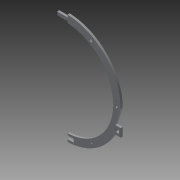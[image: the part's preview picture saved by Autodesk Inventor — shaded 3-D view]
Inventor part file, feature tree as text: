
AUTODESK INVENTOR PART (.ipt)
format: ipt  version: 2013 (Build 170138000, 138)  size: 147,968 bytes
history: native  units: in
note: dims shown in document units (in); Inventor stores cm internally (conversion verified against a paired STEP export)
features: extrude x1, sketch x1
ambient origin geometry x8: Origin, YZ Plane, XZ Plane, XY Plane, X Axis, Y Axis, Z Axis, Center Point
feature tree (2):
  extrude  "Extrusion21"  Depth=13.3in
  sketch  "Sketch1"  dims[d51=11.5in d52=13.3in d72=0.25in d73=0.2in d75=1.25in d76=0.4in d82=3.0in d86=2.5in d87=6.25in d89=0.1875in d90=0.2in d91=0.375in d92=0.4in d93=0.1875in d100=0.5in d101=0.2in d103=1.0in d104=0.4in d105=0.25in d106=0.2953in d107=1.0in d113=60.0in d114=60.0deg d115=60.0deg d121=0.125in d122=0.25in d123=6.0in d124=0.25in d125=0.125in d126=0.25in d127=0.25in d128=6.0in d130=0.25in d131=0.25in d132=0.25in d133=0.125in d134=6.0in d139=1.0in d140=0.4947in d141=0.25in d142=0.0in]
